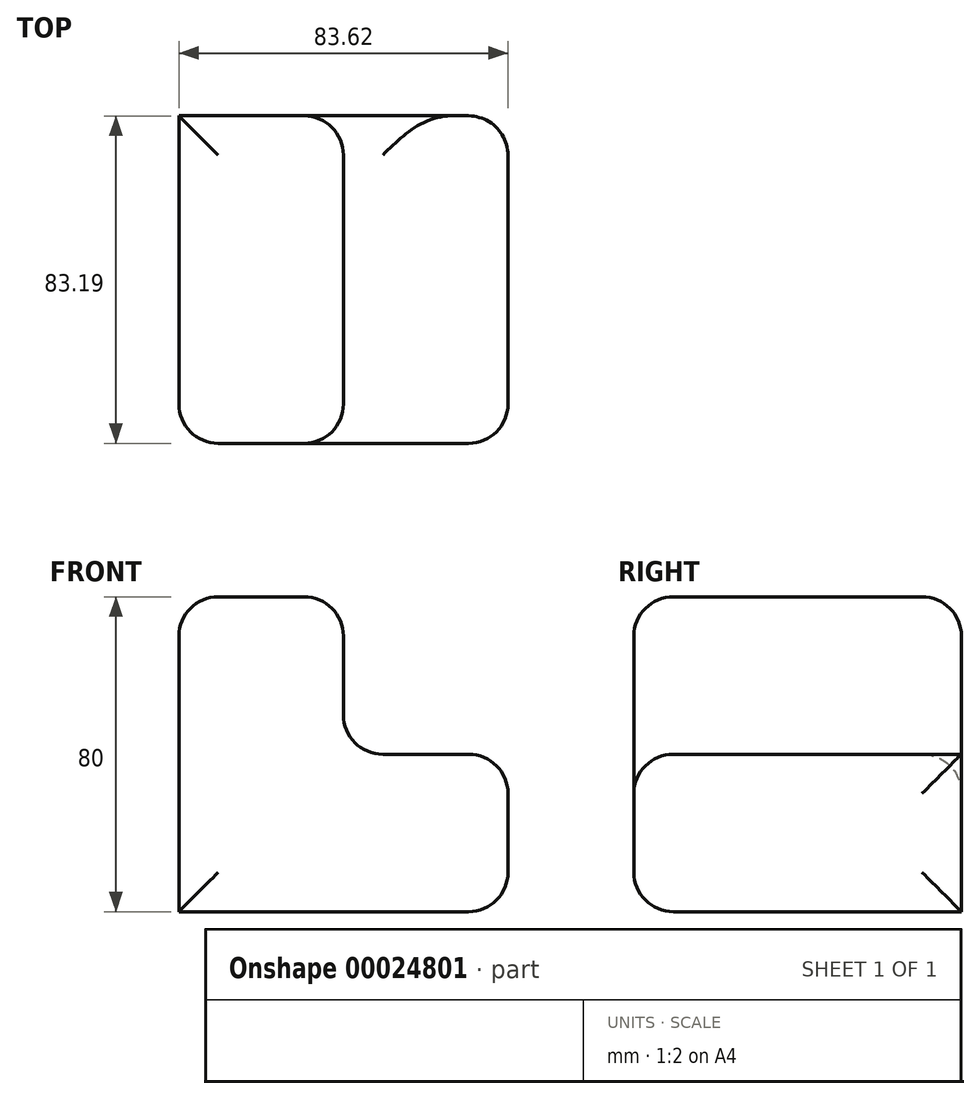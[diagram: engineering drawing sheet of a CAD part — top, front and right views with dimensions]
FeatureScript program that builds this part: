
annotation { "Feature Type Name" : "Feature", "Feature Type Description" : "" }
export const myFeature = defineFeature(function(context is Context, id is Id, definition is map)
    precondition{}
    {
        {
            var Q0;
            Q0=qCreatedBy(makeId("Top.planeOp"),FACE);
            var sketch = newSketch(context, id + "F0", { "sketchPlane" : qUnion([Q0])});
            skLineSegment(sketch, "E0.bottom", {"start": v(-59.13, -45.93) * mm, "end": v(24.5, -45.93) * mm});
            skLineSegment(sketch, "E0.top", {"start": v(-59.13, 37.26) * mm, "end": v(24.5, 37.26) * mm});
            skLineSegment(sketch, "E0.left", {"start": v(-59.13, -45.93) * mm, "end": v(-59.13, 37.26) * mm});
            skLineSegment(sketch, "E0.right", {"start": v(24.5, -45.93) * mm, "end": v(24.5, 37.26) * mm});
            skSolve(sketch);
        }
        {
            var Q0;
            Q0=makeQuery(id+"F0.imprint","IMPRINT",FACE,{"disambiguationData":[TD([[makeQuery(id+"F0.imprint","IMPRINT",EDGE,{"derivedFrom":sQuery(id+"F0.wireOp",EDGE,"E0.bottom")}),1.0]])]});
            extrude(context, id + "F1", {"entities" : qUnion([Q0]), "depth" : 40 * mm});
        }
        {
            var Q0;
            Q0=makeQuery(id+"F1.opExtrude","CAP_FACE",FACE,{"disambiguationData":[OSD([sQuery(id+"F0.wireOp",EDGE,"E0.bottom"),sQuery(id+"F0.wireOp",EDGE,"E0.top"),sQuery(id+"F0.wireOp",EDGE,"E0.left"),sQuery(id+"F0.wireOp",EDGE,"E0.right")])],"isStart":false});
            var sketch = newSketch(context, id + "F2", { "sketchPlane" : qUnion([Q0])});
            skLineSegment(sketch, "E1", {"start": v(-17.32, 37.26) * mm, "end": v(-17.32, -45.93) * mm});
            skSolve(sketch);
        }
        {
            var Q0;
            {var subQ1=sQuery(id+"F2.wireOp",EDGE,"E1");Q0=makeQuery(id+"F2.imprint","IMPRINT",FACE,{"disambiguationData":[TD([[makeQuery(id+"F2.imprint","IMPRINT",EDGE,{"derivedFrom":subQ1}),-1.0]])]});}
            extrude(context, id + "F3", {"entities" : qUnion([Q0]), "operationType" : NewBodyOperationType.ADD, "depth" : 40 * mm});
        }
        {
            var Q0;
            Q0=makeQuery(id+"F3.opExtrude","CAP_FACE",FACE,{"disambiguationData":[OSD([sQuery(id+"F0.wireOp",EDGE,"E0.bottom"),sQuery(id+"F0.wireOp",EDGE,"E0.top"),sQuery(id+"F0.wireOp",EDGE,"E0.left"),sQuery(id+"F2.wireOp",EDGE,"E1")])],"isStart":false});
            var Q1;
            Q1=makeQuery(id+"F3.opExtrude","SWEPT_FACE",FACE,{"disambiguationData":[OSD([sQuery(id+"F2.wireOp",EDGE,"E1")])]});
            var Q2;
            {var subQ0=sQuery(id+"F0.wireOp",EDGE,"E0.bottom");Q2=makeQuery(id+"F3.boolean.opBoolean","MERGE",FACE,{"derivedFrom":[makeQuery(id+"F1.opExtrude","SWEPT_FACE",FACE,{"disambiguationData":[OSD([subQ0])]}),makeQuery(id+"F3.opExtrude","SWEPT_FACE",FACE,{"disambiguationData":[OSD([subQ0])]})]});}
            var Q3;
            Q3=makeQuery(id+"F1.opExtrude","SWEPT_FACE",FACE,{"disambiguationData":[OSD([sQuery(id+"F0.wireOp",EDGE,"E0.right")])]});
            fillet(context, id + "F4", {"entities" : qUnion([Q0, Q1, Q2, Q3]), "radius" : 10 * mm, "tangentPropagation" : true, "allowEdgeOverflow" : false});
        }
    });
